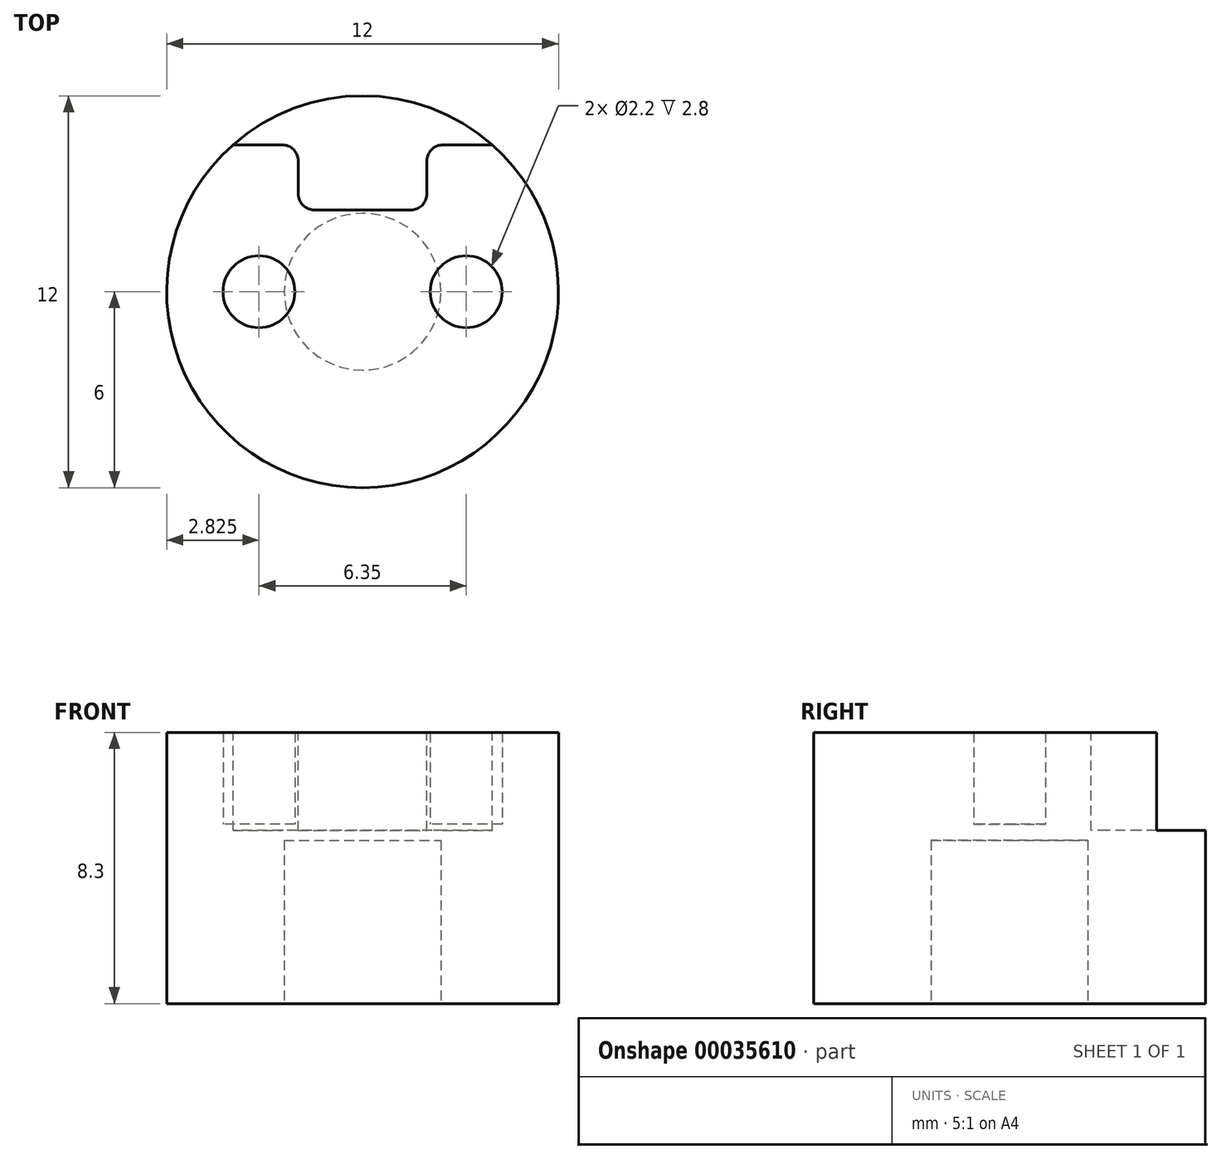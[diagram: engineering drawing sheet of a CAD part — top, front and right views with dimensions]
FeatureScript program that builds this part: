
annotation { "Feature Type Name" : "Feature", "Feature Type Description" : "" }
export const myFeature = defineFeature(function(context is Context, id is Id, definition is map)
    precondition{}
    {
        {
            var Q0;
            Q0=qCreatedBy(makeId("Top.planeOp"),FACE);
            var sketch = newSketch(context, id + "F0", { "sketchPlane" : qUnion([Q0])});
            skCircle(sketch, "E0", {"center": v(-3.18, 0) * mm, "radius": 1.1 * mm});
            skCircle(sketch, "E1", {"center": v(3.18, 0) * mm, "radius": 1.1 * mm});
            skCircle(sketch, "E2", {"center": v(0, 0) * mm, "radius": 6 * mm});
            skSolve(sketch);
        }
        {
            var Q0;
            Q0=qSketchRegion(id+"F0",true);
            extrude(context, id + "F1", {"entities" : qUnion([Q0]), "offsetDistance" : 25 * mm, "depth" : 2.8 * mm});
        }
        {
            var Q0;
            Q0=makeQuery(id+"F1.opExtrude","CAP_FACE",FACE,{"disambiguationData":[OSD([sQuery(id+"F0.wireOp",EDGE,"E0"),sQuery(id+"F0.wireOp",EDGE,"E1"),sQuery(id+"F0.wireOp",EDGE,"E2"),sQuery(id+"F0.wireOp",EDGE,"mxWlrIbW-bbLS-1jjZ-dLkJ-aSx3uFq2Umk3")])],"isStart":true});
            var sketch = newSketch(context, id + "F2", { "sketchPlane" : qUnion([Q0])});
            skCircle(sketch, "E3.0", {"center": v(0, 0) * mm, "radius": 6 * mm});
            skSolve(sketch);
        }
        {
            var Q0;
            Q0=qSketchRegion(id+"F2",true);
            extrude(context, id + "F3", {"entities" : qUnion([Q0]), "operationType" : NewBodyOperationType.ADD, "depth" : 5.5 * mm});
        }
        {
            var Q0;
            Q0=makeQuery(id+"F1.opExtrude","CAP_FACE",FACE,{"disambiguationData":[OSD([sQuery(id+"F0.wireOp",EDGE,"E0"),sQuery(id+"F0.wireOp",EDGE,"E1"),sQuery(id+"F0.wireOp",EDGE,"E2"),sQuery(id+"F0.wireOp",EDGE,"mxWlrIbW-bbLS-1jjZ-dLkJ-aSx3uFq2Umk3")])],"isStart":false});
            var sketch = newSketch(context, id + "F4", { "sketchPlane" : qUnion([Q0])});
            skLineSegment(sketch, "E4", {"start": v(-3.97, 4.5) * mm, "end": v(-1.97, 4.5) * mm});
            skLineSegment(sketch, "E5", {"start": v(-1.97, 4.5) * mm, "end": v(-1.97, 2.5) * mm});
            skLineSegment(sketch, "E6", {"start": v(-1.97, 2.5) * mm, "end": v(1.97, 2.5) * mm});
            skLineSegment(sketch, "E7", {"start": v(1.97, 2.5) * mm, "end": v(1.97, 4.5) * mm});
            skLineSegment(sketch, "E8", {"start": v(1.97, 4.5) * mm, "end": v(3.97, 4.5) * mm});
            skCircle(sketch, "E9.0", {"center": v(0, 0) * mm, "radius": 6 * mm});
            skSolve(sketch);
        }
        {
            var Q0;
            {var subQ1=sQuery(id+"F4.wireOp",EDGE,"E4");Q0=makeQuery(id+"F4.imprint","IMPRINT",FACE,{"disambiguationData":[TD([[makeQuery(id+"F4.imprint","IMPRINT",EDGE,{"derivedFrom":subQ1}),1.0]])]});}
            extrude(context, id + "F5", {"entities" : qUnion([Q0]), "operationType" : NewBodyOperationType.REMOVE, "oppositeDirection" : true, "depth" : 3 * mm});
        }
        {
            var Q0;
            Q0=makeQuery(id+"F5.boolean.opBoolean","COPY",EDGE,{"derivedFrom":makeQuery(id+"F5.opExtrude","SWEPT_EDGE",EDGE,{"disambiguationData":[OSD([sQuery(id+"F4.wireOp",EDGE,"E4"),sQuery(id+"F4.wireOp",EDGE,"E9.0")])]})});
            var Q1;
            Q1=makeQuery(id+"F5.boolean.opBoolean","COPY",EDGE,{"derivedFrom":makeQuery(id+"F5.opExtrude","SWEPT_EDGE",EDGE,{"disambiguationData":[OSD([sQuery(id+"F4.wireOp",EDGE,"E4"),sQuery(id+"F4.wireOp",EDGE,"E5")])]})});
            var Q2;
            Q2=makeQuery(id+"F5.boolean.opBoolean","COPY",EDGE,{"derivedFrom":makeQuery(id+"F5.opExtrude","SWEPT_EDGE",EDGE,{"disambiguationData":[OSD([sQuery(id+"F4.wireOp",EDGE,"E6"),sQuery(id+"F4.wireOp",EDGE,"E7")])]})});
            var Q3;
            Q3=makeQuery(id+"F5.boolean.opBoolean","COPY",EDGE,{"derivedFrom":makeQuery(id+"F5.opExtrude","SWEPT_EDGE",EDGE,{"disambiguationData":[OSD([sQuery(id+"F4.wireOp",EDGE,"E7"),sQuery(id+"F4.wireOp",EDGE,"E8")])]})});
            var Q4;
            Q4=makeQuery(id+"F5.boolean.opBoolean","COPY",EDGE,{"derivedFrom":makeQuery(id+"F5.opExtrude","SWEPT_EDGE",EDGE,{"disambiguationData":[OSD([sQuery(id+"F4.wireOp",EDGE,"E8"),sQuery(id+"F4.wireOp",EDGE,"E9.0")])]})});
            var Q5;
            Q5=makeQuery(id+"F5.boolean.opBoolean","COPY",EDGE,{"derivedFrom":makeQuery(id+"F5.opExtrude","SWEPT_EDGE",EDGE,{"disambiguationData":[OSD([sQuery(id+"F4.wireOp",EDGE,"E5"),sQuery(id+"F4.wireOp",EDGE,"E6")])]})});
            fillet(context, id + "F6", {"entities" : qUnion([Q0, Q1, Q2, Q3, Q4, Q5]), "radius" : .5 * mm, "tangentPropagation" : true, "allowEdgeOverflow" : false});
        }
        {
            var Q0;
            Q0=makeQuery(id+"F3.opExtrude","CAP_FACE",FACE,{"disambiguationData":[OSD([sQuery(id+"F2.wireOp",EDGE,"E3.0")])],"isStart":false});
            var sketch = newSketch(context, id + "F7", { "sketchPlane" : qUnion([Q0])});
            skCircle(sketch, "E10", {"center": v(0, 0) * mm, "radius": 2.4 * mm});
            skSolve(sketch);
        }
        {
            var Q0;
            Q0=qSketchRegion(id+"F7",true);
            extrude(context, id + "F8", {"entities" : qUnion([Q0]), "operationType" : NewBodyOperationType.REMOVE, "oppositeDirection" : true, "depth" : 5 * mm, "offsetDistance" : 25 * mm});
        }
    });
